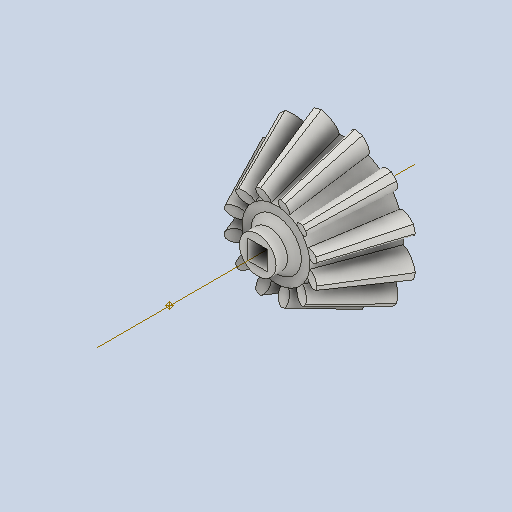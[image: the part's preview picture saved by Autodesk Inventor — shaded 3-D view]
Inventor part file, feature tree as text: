
AUTODESK INVENTOR PART (.ipt)
format: ipt  version: 2022 (Build 260153000, 153)  size: 511,488 bytes
history: native  units: in
note: dims shown in document units (in); Inventor stores cm internally (conversion verified against a paired STEP export)
features: other x30, sketch x3
ambient origin geometry x8: Origin, YZ Plane, XZ Plane, XY Plane, X Axis, Y Axis, Z Axis, Center Point
bodies: Solid1 (feature_tree)
feature tree (33):
  other  "Bevel Gear11_MIR1.ipt"
  other  "Solid1::Bevel Gear11_MIR1.ipt"
  other  "TaggingFeature1"
  other  "Teeth Body Sketch"
  other  "Start Sketch"
  other  "End Sketch"
  other  "End Sketch Right"
  other  "End Sketch Left"
  other  "Body Sketch"
  sketch  "Sketch6"  dims[d0=0.3937in]
  sketch  "Sketch8"  dims[d48=0.0in]
  sketch  "Sketch9"  dims[d49=0.0in d50=90.0deg d52=0.0in d53=0.0in d54=0.0in]
  other  "3D Sketch Right"
  other  "3D Sketch Left"
  other  "Mesh Plane"
  other  "Top Plane"
  other  "Mesh Plane2"
  other  "Tooth Plane"
  other  "End Plane"
  other  "End Plane Right"
  other  "End Plane Left"
  other  "Z Axis_1"
  other  "Top Point"
  other  "Start Point"
  other  "End Point"
  other  "Srf1"
  other  "Srf1::Derived"
  other  "Start plane iMate"
  other  "Mesh iMate2"
  other  "Axis Angle iMate"
  other  "Axis iMate"
  other  "Mesh iMate"
  other  "Intersection iMate"
